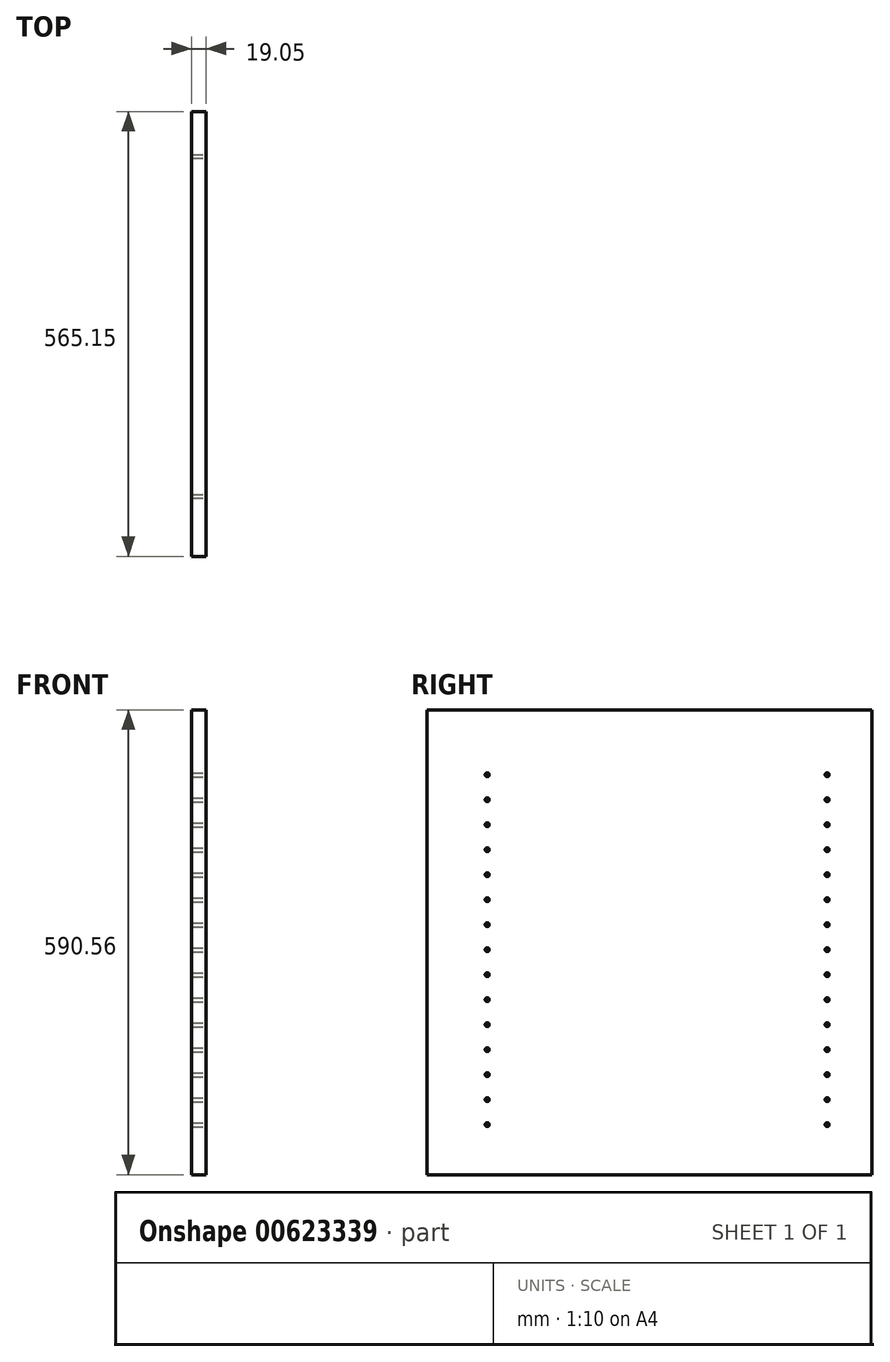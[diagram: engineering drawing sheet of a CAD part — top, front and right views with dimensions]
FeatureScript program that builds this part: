
annotation { "Feature Type Name" : "Feature", "Feature Type Description" : "" }
export const myFeature = defineFeature(function(context is Context, id is Id, definition is map)
    precondition{}
    {
        {
            var Q0;
            Q0=qCreatedBy(makeId("Right.planeOp"),FACE);
            var sketch = newSketch(context, id + "F0", { "sketchPlane" : qUnion([Q0])});
            skLineSegment(sketch, "E0.bottom", {"start": v(292.1, 295.28) * mm, "end": v(-292.1, 295.28) * mm});
            skLineSegment(sketch, "E0.top", {"start": v(292.1, -295.28) * mm, "end": v(-292.1, -295.28) * mm});
            skLineSegment(sketch, "E0.left", {"start": v(292.1, 295.28) * mm, "end": v(292.1, -295.28) * mm});
            skLineSegment(sketch, "E0.right", {"start": v(-292.1, 295.28) * mm, "end": v(-292.1, -295.28) * mm});
            skPoint(sketch, "E0.middle", {"position": v(0, 0) * mm});
            skSolve(sketch);
        }
        {
            var Q0;
            Q0=makeQuery(id+"F0.imprint","IMPRINT",FACE,{"disambiguationData":[TD([[makeQuery(id+"F0.imprint","IMPRINT",EDGE,{"derivedFrom":sQuery(id+"F0.wireOp",EDGE,"E0.bottom")}),1.0]])]});
            extrude(context, id + "F1", {"entities" : qUnion([Q0]), "depth" : 19.05 * mm, "offsetDistance" : 25.4 * mm});
        }
        {
            var Q0;
            Q0=makeQuery(id+"F1.opExtrude","CAP_FACE",FACE,{"disambiguationData":[OSD([sQuery(id+"F0.wireOp",EDGE,"E0.bottom"),sQuery(id+"F0.wireOp",EDGE,"E0.top"),sQuery(id+"F0.wireOp",EDGE,"E0.left"),sQuery(id+"F0.wireOp",EDGE,"E0.right")])],"isStart":false});
            var sketch = newSketch(context, id + "F2", { "sketchPlane" : qUnion([Q0])});
            skLineSegment(sketch, "E1", {"start": v(0, 295.28) * mm, "end": v(0, 180.97) * mm});
            skPoint(sketch, "E1.endSnap0", {"position": v(0, 295.28) * mm});
            skLineSegment(sketch, "E2.bottom", {"start": v(215.9, 149.23) * mm, "end": v(-215.9, 149.23) * mm});
            skLineSegment(sketch, "E2.top", {"start": v(215.9, 212.73) * mm, "end": v(-215.9, 212.72) * mm});
            skLineSegment(sketch, "E2.left", {"start": v(215.9, 149.23) * mm, "end": v(215.9, 212.73) * mm});
            skLineSegment(sketch, "E2.right", {"start": v(-215.9, 149.23) * mm, "end": v(-215.9, 212.72) * mm});
            skPoint(sketch, "E2.middle", {"position": v(0, 180.97) * mm});
            skLineSegment(sketch, "E3", {"start": v(0, 149.23) * mm, "end": v(0, 85.73) * mm});
            skLineSegment(sketch, "E4.bottom", {"start": v(215.9, 53.98) * mm, "end": v(-215.9, 53.97) * mm});
            skLineSegment(sketch, "E4.top", {"start": v(215.9, 117.48) * mm, "end": v(-215.9, 117.47) * mm});
            skLineSegment(sketch, "E4.left", {"start": v(215.9, 53.98) * mm, "end": v(215.9, 117.48) * mm});
            skLineSegment(sketch, "E4.right", {"start": v(-215.9, 53.97) * mm, "end": v(-215.9, 117.47) * mm});
            skPoint(sketch, "E4.middle", {"position": v(0, 85.73) * mm});
            skLineSegment(sketch, "E5", {"start": v(0, 53.97) * mm, "end": v(0, -9.53) * mm});
            skLineSegment(sketch, "E6.bottom", {"start": v(215.9, -41.27) * mm, "end": v(-215.9, -41.28) * mm});
            skLineSegment(sketch, "E6.top", {"start": v(215.9, 22.23) * mm, "end": v(-215.9, 22.22) * mm});
            skLineSegment(sketch, "E6.left", {"start": v(215.9, -41.27) * mm, "end": v(215.9, 22.23) * mm});
            skLineSegment(sketch, "E6.right", {"start": v(-215.9, -41.28) * mm, "end": v(-215.9, 22.22) * mm});
            skPoint(sketch, "E6.middle", {"position": v(0, -9.53) * mm});
            skLineSegment(sketch, "E7", {"start": v(0, -41.27) * mm, "end": v(0, -104.77) * mm});
            skLineSegment(sketch, "E8.bottom", {"start": v(-215.9, -73.02) * mm, "end": v(215.9, -73.02) * mm});
            skLineSegment(sketch, "E8.top", {"start": v(-215.9, -136.52) * mm, "end": v(215.9, -136.52) * mm});
            skLineSegment(sketch, "E8.left", {"start": v(-215.9, -73.02) * mm, "end": v(-215.9, -136.52) * mm});
            skLineSegment(sketch, "E8.right", {"start": v(215.9, -73.02) * mm, "end": v(215.9, -136.52) * mm});
            skPoint(sketch, "E8.middle", {"position": v(0, -104.77) * mm});
            skLineSegment(sketch, "E9", {"start": v(0, -136.52) * mm, "end": v(0, -200.02) * mm});
            skLineSegment(sketch, "E10.bottom", {"start": v(-215.9, -168.27) * mm, "end": v(215.9, -168.27) * mm});
            skLineSegment(sketch, "E10.top", {"start": v(-215.9, -231.77) * mm, "end": v(215.9, -231.77) * mm});
            skLineSegment(sketch, "E10.left", {"start": v(-215.9, -168.27) * mm, "end": v(-215.9, -231.77) * mm});
            skLineSegment(sketch, "E10.right", {"start": v(215.9, -168.27) * mm, "end": v(215.9, -231.77) * mm});
            skPoint(sketch, "E10.middle", {"position": v(0, -200.02) * mm});
            skPoint(sketch, "E11", {"position": v(-215.9, 212.72) * mm});
            skPoint(sketch, "E12", {"position": v(-215.9, 180.97) * mm});
            skPoint(sketch, "E13", {"position": v(-215.9, 149.23) * mm});
            skPoint(sketch, "E14", {"position": v(-215.9, 117.47) * mm});
            skPoint(sketch, "E15", {"position": v(-215.9, 85.72) * mm});
            skPoint(sketch, "E16", {"position": v(-215.9, 53.97) * mm});
            skPoint(sketch, "E17", {"position": v(-215.9, 22.22) * mm});
            skPoint(sketch, "E18", {"position": v(-215.9, -9.53) * mm});
            skPoint(sketch, "E19", {"position": v(-215.9, -41.28) * mm});
            skPoint(sketch, "E20", {"position": v(-215.9, -73.02) * mm});
            skPoint(sketch, "E21", {"position": v(-215.9, -104.77) * mm});
            skPoint(sketch, "E22", {"position": v(-215.9, -136.52) * mm});
            skPoint(sketch, "E23", {"position": v(-215.9, -168.27) * mm});
            skPoint(sketch, "E24", {"position": v(-215.9, -200.02) * mm});
            skPoint(sketch, "E25", {"position": v(-215.9, -231.77) * mm});
            skPoint(sketch, "E26", {"position": v(215.9, -231.77) * mm});
            skPoint(sketch, "E27", {"position": v(215.9, -200.02) * mm});
            skPoint(sketch, "E28", {"position": v(215.9, -168.27) * mm});
            skPoint(sketch, "E29", {"position": v(215.9, -136.52) * mm});
            skPoint(sketch, "E30", {"position": v(215.9, -104.77) * mm});
            skPoint(sketch, "E31", {"position": v(215.9, -73.02) * mm});
            skPoint(sketch, "E32", {"position": v(215.9, -41.27) * mm});
            skPoint(sketch, "E33", {"position": v(215.9, -9.52) * mm});
            skPoint(sketch, "E34", {"position": v(215.9, 22.23) * mm});
            skPoint(sketch, "E35", {"position": v(215.9, 53.98) * mm});
            skPoint(sketch, "E36", {"position": v(215.9, 85.73) * mm});
            skPoint(sketch, "E37", {"position": v(215.9, 117.48) * mm});
            skPoint(sketch, "E38", {"position": v(215.9, 149.23) * mm});
            skPoint(sketch, "E39", {"position": v(215.9, 180.98) * mm});
            skPoint(sketch, "E40", {"position": v(215.9, 212.73) * mm});
            skSolve(sketch);
        }
        {
            var Q0;
            Q0=sQuery(id+"F2.wireOp",VERTEX,"E11");
            var Q1;
            Q1=sQuery(id+"F2.wireOp",VERTEX,"E12");
            var Q2;
            Q2=sQuery(id+"F2.wireOp",VERTEX,"E13");
            var Q3;
            Q3=sQuery(id+"F2.wireOp",VERTEX,"E14");
            var Q4;
            Q4=sQuery(id+"F2.wireOp",VERTEX,"E15");
            var Q5;
            Q5=sQuery(id+"F2.wireOp",VERTEX,"E16");
            var Q6;
            Q6=sQuery(id+"F2.wireOp",VERTEX,"E17");
            var Q7;
            Q7=sQuery(id+"F2.wireOp",VERTEX,"E18");
            var Q8;
            Q8=sQuery(id+"F2.wireOp",VERTEX,"E19");
            var Q9;
            Q9=sQuery(id+"F2.wireOp",VERTEX,"E20");
            var Q10;
            Q10=sQuery(id+"F2.wireOp",VERTEX,"E21");
            var Q11;
            Q11=sQuery(id+"F2.wireOp",VERTEX,"E22");
            var Q12;
            Q12=sQuery(id+"F2.wireOp",VERTEX,"E23");
            var Q13;
            Q13=sQuery(id+"F2.wireOp",VERTEX,"E24");
            var Q14;
            Q14=sQuery(id+"F2.wireOp",VERTEX,"E25");
            var Q15;
            Q15=sQuery(id+"F2.wireOp",VERTEX,"E26");
            var Q16;
            Q16=sQuery(id+"F2.wireOp",VERTEX,"E27");
            var Q17;
            Q17=sQuery(id+"F2.wireOp",VERTEX,"E28");
            var Q18;
            Q18=sQuery(id+"F2.wireOp",VERTEX,"E29");
            var Q19;
            Q19=sQuery(id+"F2.wireOp",VERTEX,"E30");
            var Q20;
            Q20=sQuery(id+"F2.wireOp",VERTEX,"E31");
            var Q21;
            Q21=sQuery(id+"F2.wireOp",VERTEX,"E32");
            var Q22;
            Q22=sQuery(id+"F2.wireOp",VERTEX,"E33");
            var Q23;
            Q23=sQuery(id+"F2.wireOp",VERTEX,"E34");
            var Q24;
            Q24=sQuery(id+"F2.wireOp",VERTEX,"E35");
            var Q25;
            Q25=sQuery(id+"F2.wireOp",VERTEX,"E36");
            var Q26;
            Q26=sQuery(id+"F2.wireOp",VERTEX,"E37");
            var Q27;
            Q27=sQuery(id+"F2.wireOp",VERTEX,"E38");
            var Q28;
            Q28=sQuery(id+"F2.wireOp",VERTEX,"E39");
            var Q29;
            Q29=sQuery(id+"F2.wireOp",VERTEX,"E40");
            var Q30;
            Q30=makeQuery(id+"F1.opExtrude","SWEPT_BODY",BODY,{"disambiguationData":[OSD([sQuery(id+"F0.wireOp",EDGE,"E0.bottom"),sQuery(id+"F0.wireOp",EDGE,"E0.top"),sQuery(id+"F0.wireOp",EDGE,"E0.left"),sQuery(id+"F0.wireOp",EDGE,"E0.right")])]});
            hole(context, id + "F3", {"style" : HoleStyle.SIMPLE, "endStyle" : HoleEndStyle.BLIND, "holeDiameter" : 5 * mm, "majorDiameter" : 6.35 * mm, "holeDepth" : 1905 * mm, "isTappedThrough" : true, "tappedDepth" : 12.7 * mm, "tapClearance" : 3, "startFromSketch" : true, "locations" : qUnion([Q0, Q1, Q2, Q3, Q4, Q5, Q6, Q7, Q8, Q9, Q10, Q11, Q12, Q13, Q14, Q15, Q16, Q17, Q18, Q19, Q20, Q21, Q22, Q23, Q24, Q25, Q26, Q27, Q28, Q29]), "scope" : qUnion([Q30])});
        }
        {
            var Q0;
            Q0=makeQuery(id+"F1.opExtrude","SWEPT_FACE",FACE,{"disambiguationData":[OSD([sQuery(id+"F0.wireOp",EDGE,"E0.left")])]});
            extrude(context, id + "F4", {"entities" : qUnion([Q0]), "operationType" : NewBodyOperationType.REMOVE, "oppositeDirection" : true, "depth" : 19.05 * mm, "offsetDistance" : 25.4 * mm});
        }
    });
